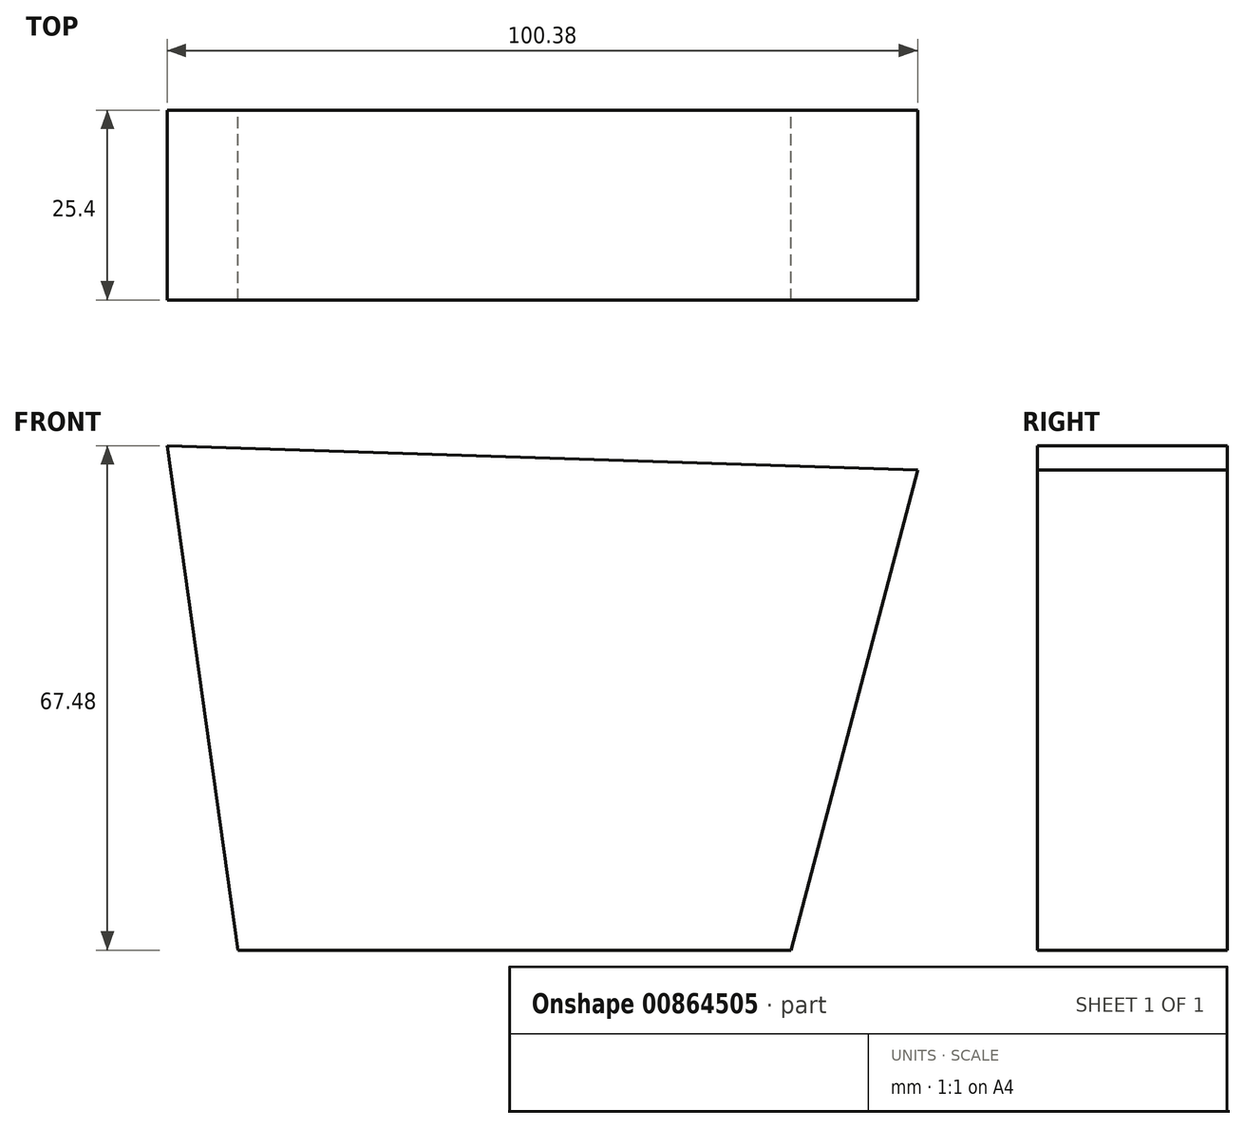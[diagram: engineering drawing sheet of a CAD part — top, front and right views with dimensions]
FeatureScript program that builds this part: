
annotation { "Feature Type Name" : "Feature", "Feature Type Description" : "" }
export const myFeature = defineFeature(function(context is Context, id is Id, definition is map)
    precondition{}
    {
        {
            var Q0;
            Q0=qCreatedBy(makeId("Front.planeOp"),FACE);
            var sketch = newSketch(context, id + "F0", { "sketchPlane" : qUnion([Q0])});
            skLineSegment(sketch, "E0", {"start": v(-69.86, 32.23) * mm, "end": v(30.52, 28.99) * mm});
            skLineSegment(sketch, "E1", {"start": v(30.52, 28.99) * mm, "end": v(13.57, -35.25) * mm});
            skLineSegment(sketch, "E2", {"start": v(13.57, -35.25) * mm, "end": v(-60.36, -35.25) * mm});
            skLineSegment(sketch, "E3", {"start": v(-60.36, -35.25) * mm, "end": v(-69.86, 32.23) * mm});
            skSolve(sketch);
        }
        {
            var Q0;
            Q0 = qSketchRegion(id + "F0", true);
            extrude(context, id + "F1", {"entities" : qUnion([Q0]), "depth" : 25.4 * mm, "offsetDistance" : 25.4 * mm});
        }
    });
